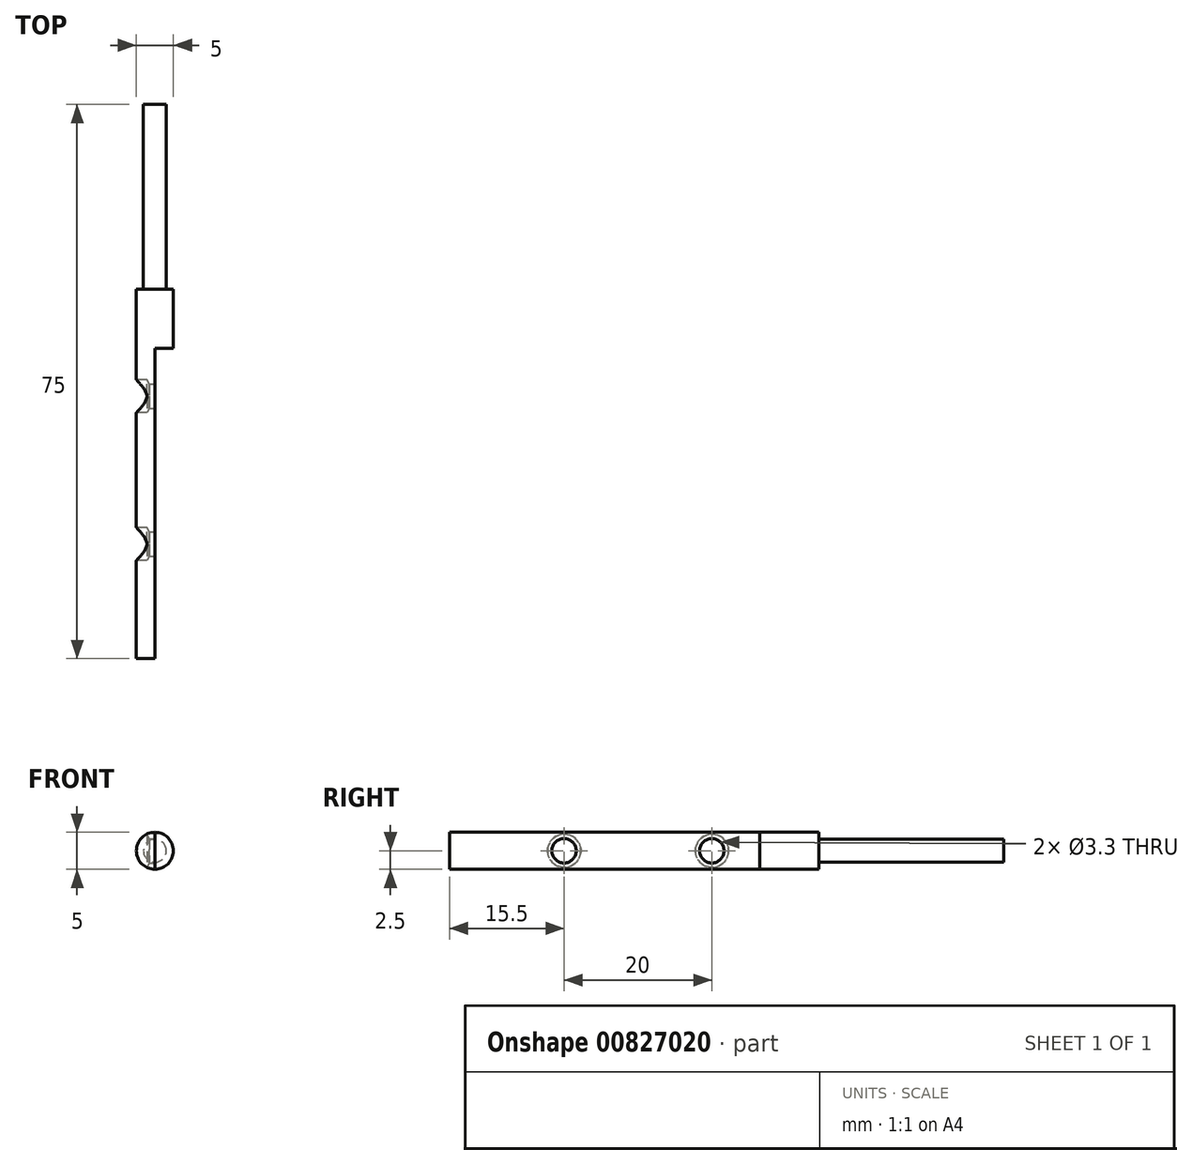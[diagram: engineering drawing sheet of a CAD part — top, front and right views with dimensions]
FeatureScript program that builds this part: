
annotation { "Feature Type Name" : "Feature", "Feature Type Description" : "" }
export const myFeature = defineFeature(function(context is Context, id is Id, definition is map)
    precondition{}
    {
        {
            var Q0;
            Q0=qCreatedBy(makeId("Front.planeOp"),FACE);
            var sketch = newSketch(context, id + "F0", { "sketchPlane" : qUnion([Q0])});
            skCircle(sketch, "E0", {"center": v(0, 0) * mm, "radius": 2.5 * mm});
            skSolve(sketch);
        }
        {
            var Q0;
            Q0 = qSketchRegion(id + "F0", true);
            extrude(context, id + "F1", {"entities" : qUnion([Q0]), "depth" : 50 * mm, "offsetDistance" : 25 * mm});
        }
        {
            var Q0;
            Q0=makeQuery(id+"F1.opExtrude","CAP_FACE",FACE,{"disambiguationData":[OSD([sQuery(id+"F0.wireOp",EDGE,"E0")])],"isStart":true});
            var sketch = newSketch(context, id + "F2", { "sketchPlane" : qUnion([Q0])});
            skCircle(sketch, "E1", {"center": v(0, 0) * mm, "radius": 1.55 * mm});
            skSolve(sketch);
        }
        {
            var Q0;
            Q0 = qSketchRegion(id + "F2", true);
            extrude(context, id + "F3", {"entities" : qUnion([Q0]), "operationType" : NewBodyOperationType.ADD, "depth" : 25 * mm, "offsetDistance" : 25 * mm});
        }
        {
            var Q0;
            Q0=makeQuery(id+"F1.opExtrude","CAP_FACE",FACE,{"disambiguationData":[OSD([sQuery(id+"F0.wireOp",EDGE,"E0")])],"isStart":false});
            var sketch = newSketch(context, id + "F4", { "sketchPlane" : qUnion([Q0])});
            skLineSegment(sketch, "E2", {"start": v(0, 2.5) * mm, "end": v(0, -2.5) * mm});
            skArc(sketch, "E3", {"start": v(0, 2.5) * mm, "mid": v(2.5, 0) * mm, "end": v(0, -2.5) * mm});
            skSolve(sketch);
        }
        {
            var Q0;
            Q0=makeQuery(id+"F4.imprint","IMPRINT",FACE,{"disambiguationData":[TD([[makeQuery(id+"F4.imprint","IMPRINT",EDGE,{"derivedFrom":sQuery(id+"F4.wireOp",EDGE,"E2")}),1.0]])]});
            extrude(context, id + "F5", {"entities" : qUnion([Q0]), "operationType" : NewBodyOperationType.REMOVE, "oppositeDirection" : true, "depth" : 42 * mm, "offsetDistance" : 25 * mm});
        }
        {
            var Q0;
            Q0=makeQuery(id+"F5.boolean.opBoolean","COPY",FACE,{"derivedFrom":makeQuery(id+"F5.opExtrude","SWEPT_FACE",FACE,{"disambiguationData":[OSD([sQuery(id+"F4.wireOp",EDGE,"E2")])]})});
            var sketch = newSketch(context, id + "F6", { "sketchPlane" : qUnion([Q0])});
            skLineSegment(sketch, "E4", {"start": v(-50, 0) * mm, "end": v(-8, 0) * mm, "construction": true});
            skLineSegment(sketch, "E5", {"start": v(-14.5, 2.5) * mm, "end": v(-14.5, -2.5) * mm, "construction": true});
            skLineSegment(sketch, "E6", {"start": v(-34.5, 2.5) * mm, "end": v(-34.5, -2.5) * mm, "construction": true});
            skPoint(sketch, "E7", {"position": v(-34.5, 0) * mm});
            skPoint(sketch, "E8", {"position": v(-14.5, 0) * mm});
            skSolve(sketch);
        }
        {
            var Q0;
            Q0=sQuery(id+"F6.wireOp",VERTEX,"E7");
            var Q1;
            Q1=sQuery(id+"F6.wireOp",VERTEX,"E8");
            var Q2;
            Q2=makeQuery(id+"F1.opExtrude","SWEPT_BODY",BODY,{"disambiguationData":[OSD([sQuery(id+"F0.wireOp",EDGE,"E0")])]});
            hole(context, id + "F7", {"style" : HoleStyle.SIMPLE, "endStyle" : HoleEndStyle.THROUGH, "standardTappedOrClearance" : lookupTablePath({ "fit" : "Normal", "standard" : "ISO", "size" : "M3", "type" : "Clearance" }), "standardBlindInLast" : lookupTablePath({ "fit" : "Standard", "standard" : "ISO", "size" : "M3", "type" : "Clearance" }), "holeDiameter" : 3.3 * mm, "majorDiameter" : 5 * mm, "isTappedThrough" : true, "tappedDepth" : 12 * mm, "tapClearance" : 3, "startFromSketch" : true, "locations" : qUnion([Q0, Q1]), "scope" : qUnion([Q2])});
        }
        {
            var Q0;
            Q0=qCreatedBy(makeId("Right.planeOp"),FACE);
            cPlane(context, id + "F8", {"entities" : qUnion([Q0]), "cplaneType" : CPlaneType.OFFSET, "offset" : 2.5 * mm, "oppositeDirection" : true, "width" : 150 * mm, "height" : 150 * mm});
        }
        {
            var Q0;
            Q0=qCreatedBy(id+"F8.planeOp",FACE);
            var sketch = newSketch(context, id + "F9", { "sketchPlane" : qUnion([Q0])});
            skPoint(sketch, "E9", {"position": v(-34.49, 0) * mm});
            skPoint(sketch, "E10", {"position": v(-14.49, 0) * mm});
            skSolve(sketch);
        }
        {
            var Q0;
            Q0=sQuery(id+"F9.wireOp",VERTEX,"E9");
            var Q1;
            Q1=sQuery(id+"F9.wireOp",VERTEX,"E10");
            var Q2;
            Q2=makeQuery(id+"F1.opExtrude","SWEPT_BODY",BODY,{"disambiguationData":[OSD([sQuery(id+"F0.wireOp",EDGE,"E0")])]});
            hole(context, id + "F10", {"style" : HoleStyle.SIMPLE, "endStyle" : HoleEndStyle.BLIND, "oppositeDirection" : true, "holeDiameter" : 4.5 * mm, "majorDiameter" : 5 * mm, "holeDepth" : 1.4 * mm, "isTappedThrough" : true, "tappedDepth" : 12 * mm, "tapClearance" : 3, "startFromSketch" : true, "locations" : qUnion([Q0, Q1]), "scope" : qUnion([Q2])});
        }
    });
